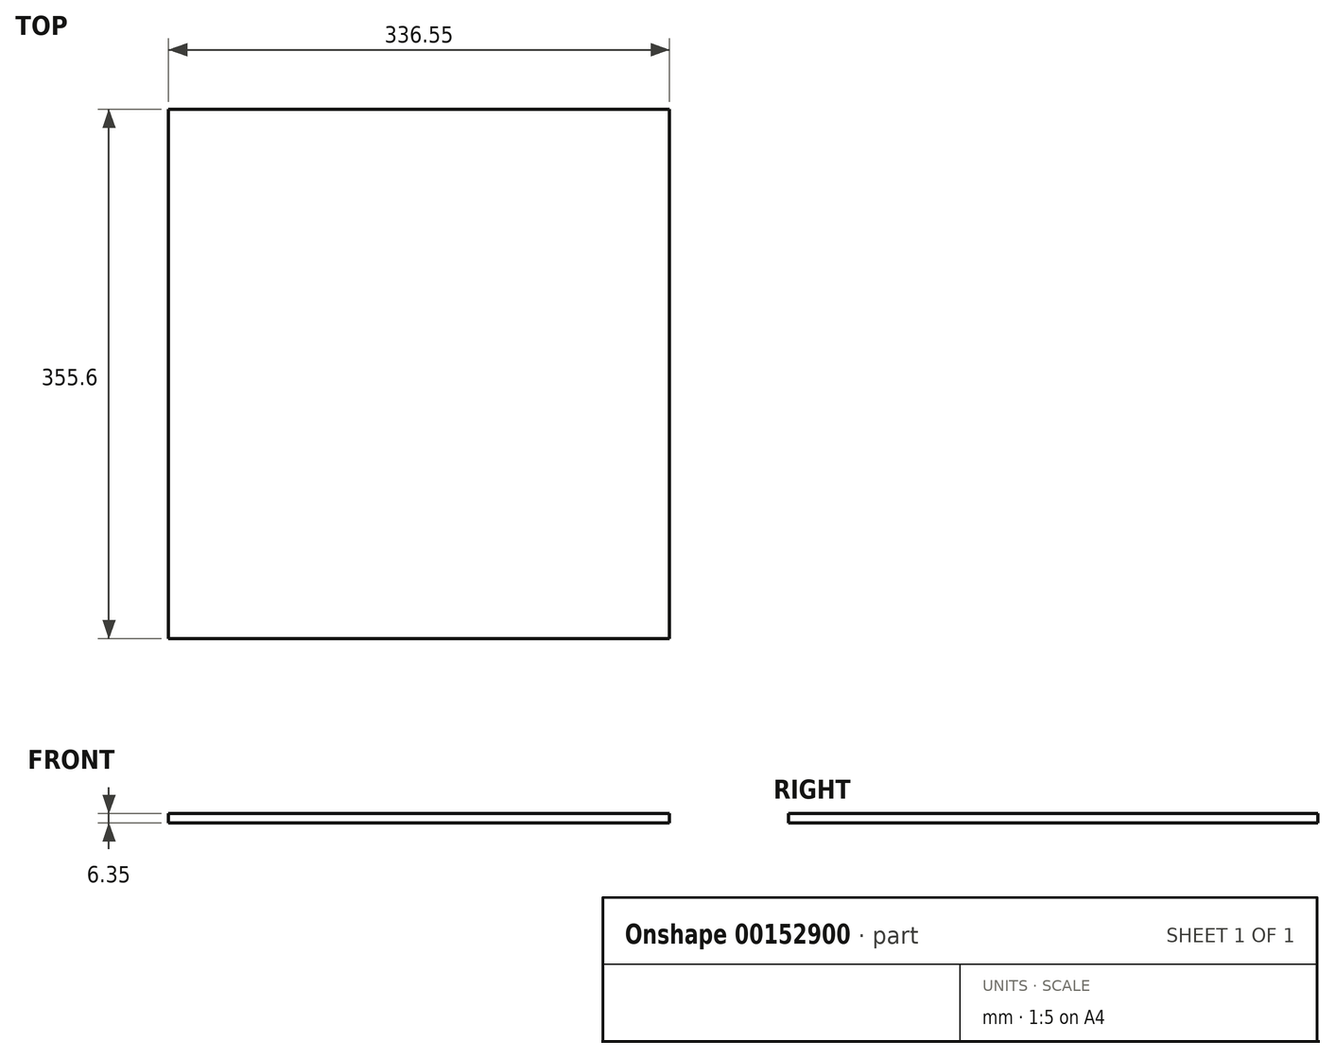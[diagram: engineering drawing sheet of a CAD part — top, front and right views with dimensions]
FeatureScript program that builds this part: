
annotation { "Feature Type Name" : "Feature", "Feature Type Description" : "" }
export const myFeature = defineFeature(function(context is Context, id is Id, definition is map)
    precondition{}
    {
        {
            var Q0;
            Q0=qCreatedBy(makeId("Top.planeOp"),FACE);
            var sketch = newSketch(context, id + "F0", { "sketchPlane" : qUnion([Q0])});
            skLineSegment(sketch, "E0.bottom", {"start": v(0, 0) * mm, "end": v(336.55, 0) * mm});
            skLineSegment(sketch, "E0.top", {"start": v(0, -355.6) * mm, "end": v(336.55, -355.6) * mm});
            skLineSegment(sketch, "E0.left", {"start": v(0, 0) * mm, "end": v(0, -355.6) * mm});
            skLineSegment(sketch, "E0.right", {"start": v(336.55, 0) * mm, "end": v(336.55, -355.6) * mm});
            skSolve(sketch);
        }
        {
            var Q0;
            Q0=qSketchRegion(id+"F0",true);
            extrude(context, id + "F1", {"entities" : qUnion([Q0]), "depth" : 6.35 * mm});
        }
    });
